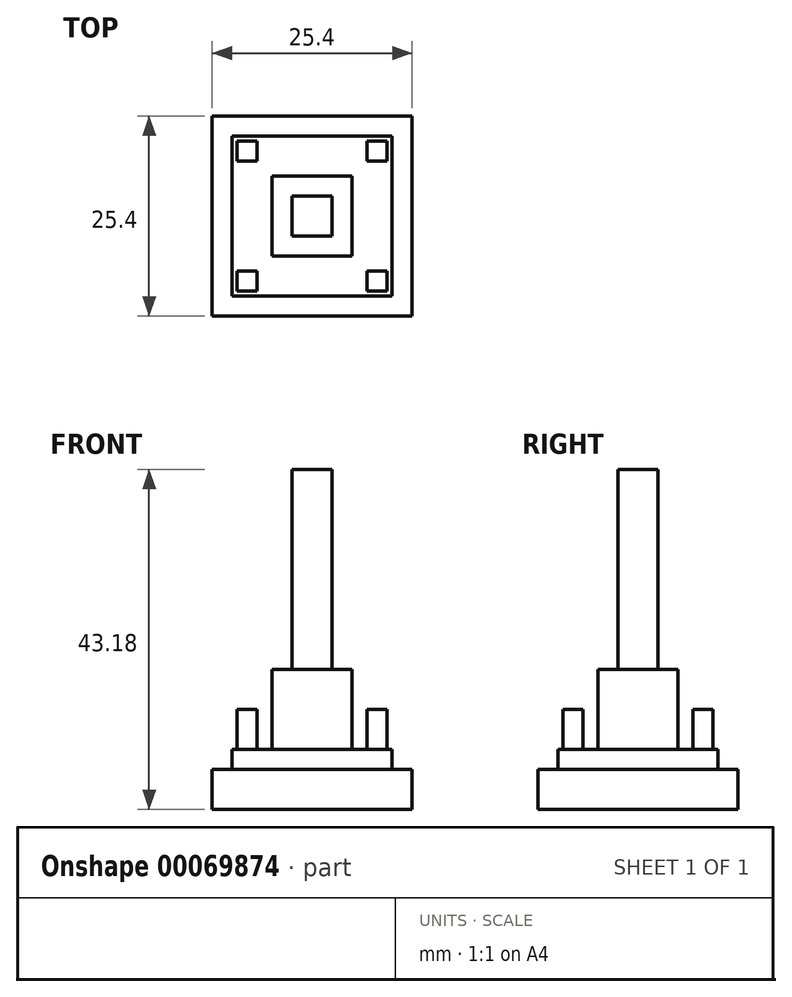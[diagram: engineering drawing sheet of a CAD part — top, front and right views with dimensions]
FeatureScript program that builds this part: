
annotation { "Feature Type Name" : "Feature", "Feature Type Description" : "" }
export const myFeature = defineFeature(function(context is Context, id is Id, definition is map)
    precondition{}
    {
        {
            var Q0;
            Q0=qCreatedBy(makeId("Top.planeOp"),FACE);
            var sketch = newSketch(context, id + "F0", { "sketchPlane" : qUnion([Q0])});
            skLineSegment(sketch, "E0.bottom", {"start": v(0, 0) * mm, "end": v(25.4, 0) * mm});
            skLineSegment(sketch, "E0.top", {"start": v(0, -25.4) * mm, "end": v(25.4, -25.4) * mm});
            skLineSegment(sketch, "E0.left", {"start": v(0, 0) * mm, "end": v(0, -25.4) * mm});
            skLineSegment(sketch, "E0.right", {"start": v(25.4, 0) * mm, "end": v(25.4, -25.4) * mm});
            skSolve(sketch);
        }
        {
            var Q0;
            Q0 = qSketchRegion(id + "F0", true);
            extrude(context, id + "F1", {"entities" : qUnion([Q0]), "depth" : 5.08 * mm});
        }
        {
            var Q0;
            Q0=makeQuery(id+"F1.opExtrude","CAP_FACE",FACE,{"disambiguationData":[OSD([sQuery(id+"F0.wireOp",EDGE,"E0.bottom"),sQuery(id+"F0.wireOp",EDGE,"E0.top"),sQuery(id+"F0.wireOp",EDGE,"E0.left"),sQuery(id+"F0.wireOp",EDGE,"E0.right")])],"isStart":false});
            var sketch = newSketch(context, id + "F2", { "sketchPlane" : qUnion([Q0])});
            skLineSegment(sketch, "E1.bottom", {"start": v(2.54, -2.54) * mm, "end": v(22.86, -2.54) * mm});
            skLineSegment(sketch, "E1.top", {"start": v(2.54, -22.86) * mm, "end": v(22.86, -22.86) * mm});
            skLineSegment(sketch, "E1.left", {"start": v(2.54, -2.54) * mm, "end": v(2.54, -22.86) * mm});
            skLineSegment(sketch, "E1.right", {"start": v(22.86, -2.54) * mm, "end": v(22.86, -22.86) * mm});
            skSolve(sketch);
        }
        {
            var Q0;
            Q0 = qSketchRegion(id + "F2", true);
            extrude(context, id + "F3", {"entities" : qUnion([Q0]), "operationType" : NewBodyOperationType.ADD, "depth" : 2.54 * mm});
        }
        {
            var Q0;
            Q0=makeQuery(id+"F3.opExtrude","CAP_FACE",FACE,{"disambiguationData":[OSD([sQuery(id+"F2.wireOp",EDGE,"E1.bottom"),sQuery(id+"F2.wireOp",EDGE,"E1.top"),sQuery(id+"F2.wireOp",EDGE,"E1.left"),sQuery(id+"F2.wireOp",EDGE,"E1.right")])],"isStart":false});
            var sketch = newSketch(context, id + "F4", { "sketchPlane" : qUnion([Q0])});
            skLineSegment(sketch, "E2.bottom", {"start": v(7.62, -17.78) * mm, "end": v(17.78, -17.78) * mm});
            skLineSegment(sketch, "E2.top", {"start": v(7.62, -7.62) * mm, "end": v(17.78, -7.62) * mm});
            skLineSegment(sketch, "E2.left", {"start": v(7.62, -17.78) * mm, "end": v(7.62, -7.62) * mm});
            skLineSegment(sketch, "E2.right", {"start": v(17.78, -17.78) * mm, "end": v(17.78, -7.62) * mm});
            skSolve(sketch);
        }
        {
            var Q0;
            Q0 = qSketchRegion(id + "F4", true);
            extrude(context, id + "F5", {"entities" : qUnion([Q0]), "operationType" : NewBodyOperationType.ADD, "depth" : 10.16 * mm});
        }
        {
            var Q0;
            Q0=makeQuery(id+"F5.opExtrude","CAP_FACE",FACE,{"disambiguationData":[OSD([sQuery(id+"F4.wireOp",EDGE,"E2.bottom"),sQuery(id+"F4.wireOp",EDGE,"E2.top"),sQuery(id+"F4.wireOp",EDGE,"E2.left"),sQuery(id+"F4.wireOp",EDGE,"E2.right")])],"isStart":false});
            var sketch = newSketch(context, id + "F6", { "sketchPlane" : qUnion([Q0])});
            skLineSegment(sketch, "E3.bottom", {"start": v(10.16, -15.24) * mm, "end": v(15.24, -15.24) * mm});
            skLineSegment(sketch, "E3.top", {"start": v(10.16, -10.16) * mm, "end": v(15.24, -10.16) * mm});
            skLineSegment(sketch, "E3.left", {"start": v(10.16, -15.24) * mm, "end": v(10.16, -10.16) * mm});
            skLineSegment(sketch, "E3.right", {"start": v(15.24, -15.24) * mm, "end": v(15.24, -10.16) * mm});
            skSolve(sketch);
        }
        {
            var Q0;
            Q0 = qSketchRegion(id + "F6", true);
            extrude(context, id + "F7", {"entities" : qUnion([Q0]), "operationType" : NewBodyOperationType.ADD, "depth" : 25.4 * mm});
        }
        {
            var Q0;
            Q0=makeQuery(id+"F3.opExtrude","CAP_FACE",FACE,{"disambiguationData":[OSD([sQuery(id+"F2.wireOp",EDGE,"E1.bottom"),sQuery(id+"F2.wireOp",EDGE,"E1.top"),sQuery(id+"F2.wireOp",EDGE,"E1.left"),sQuery(id+"F2.wireOp",EDGE,"E1.right")])],"isStart":false});
            var sketch = newSketch(context, id + "F8", { "sketchPlane" : qUnion([Q0])});
            skLineSegment(sketch, "E4.bottom", {"start": v(3.17, -3.18) * mm, "end": v(5.71, -3.18) * mm});
            skLineSegment(sketch, "E4.top", {"start": v(3.17, -5.72) * mm, "end": v(5.71, -5.72) * mm});
            skLineSegment(sketch, "E4.left", {"start": v(3.17, -3.18) * mm, "end": v(3.17, -5.72) * mm});
            skLineSegment(sketch, "E4.right", {"start": v(5.71, -3.18) * mm, "end": v(5.71, -5.72) * mm});
            skLineSegment(sketch, "E5.bottom", {"start": v(22.22, -3.18) * mm, "end": v(19.68, -3.18) * mm});
            skLineSegment(sketch, "E5.top", {"start": v(22.22, -5.72) * mm, "end": v(19.68, -5.72) * mm});
            skLineSegment(sketch, "E5.left", {"start": v(22.22, -3.18) * mm, "end": v(22.22, -5.72) * mm});
            skLineSegment(sketch, "E5.right", {"start": v(19.68, -3.18) * mm, "end": v(19.68, -5.72) * mm});
            skLineSegment(sketch, "E6.bottom", {"start": v(22.22, -22.23) * mm, "end": v(19.68, -22.23) * mm});
            skLineSegment(sketch, "E6.top", {"start": v(22.22, -19.69) * mm, "end": v(19.68, -19.69) * mm});
            skLineSegment(sketch, "E6.left", {"start": v(22.22, -22.23) * mm, "end": v(22.22, -19.69) * mm});
            skLineSegment(sketch, "E6.right", {"start": v(19.68, -22.23) * mm, "end": v(19.68, -19.69) * mm});
            skLineSegment(sketch, "E7.bottom", {"start": v(3.17, -22.23) * mm, "end": v(5.71, -22.23) * mm});
            skLineSegment(sketch, "E7.top", {"start": v(3.17, -19.69) * mm, "end": v(5.71, -19.69) * mm});
            skLineSegment(sketch, "E7.left", {"start": v(3.17, -22.23) * mm, "end": v(3.17, -19.69) * mm});
            skLineSegment(sketch, "E7.right", {"start": v(5.71, -22.23) * mm, "end": v(5.71, -19.69) * mm});
            skSolve(sketch);
        }
        {
            var Q0;
            Q0 = qSketchRegion(id + "F8", true);
            extrude(context, id + "F9", {"entities" : qUnion([Q0]), "operationType" : NewBodyOperationType.ADD, "depth" : 5.08 * mm});
        }
        {
            var Q0;
            Q0=makeQuery(id+"F9.opExtrude","SWEPT_FACE",FACE,{"disambiguationData":[OSD([sQuery(id+"F8.wireOp",EDGE,"E7.bottom")])]});
            var sketch = newSketch(context, id + "F10", { "sketchPlane" : qUnion([Q0])});
            skCircle(sketch, "E8", {"center": v(4.44, 11.43) * mm, "radius": 0.64 * mm});
            skSolve(sketch);
        }
        {
            var Q0;
            Q0 = qSketchRegion(id + "F10", true);
            extrude(context, id + "F11", {"entities" : qUnion([Q0]), "operationType" : NewBodyOperationType.ADD, "depth" : 0.25 * mm});
        }
        {
            var Q0;
            Q0=makeQuery(id+"F11.opExtrude","CAP_EDGE",EDGE,{"disambiguationData":[OSD([sQuery(id+"F10.wireOp",EDGE,"E8")])],"isStart":false});
            fillet(context, id + "F12", {"entities" : qUnion([Q0]), "radius" : 0.86 * mm, "tangentPropagation" : true, "allowEdgeOverflow" : false});
        }
        {
            var Q0;
            Q0=makeQuery(id+"F9.opExtrude","SWEPT_FACE",FACE,{"disambiguationData":[OSD([sQuery(id+"F8.wireOp",EDGE,"E7.bottom")])]});
            var sketch = newSketch(context, id + "F13", { "sketchPlane" : qUnion([Q0])});
            skCircle(sketch, "E9", {"center": v(4.44, 11.43) * mm, "radius": 2.2 * mm});
            skSolve(sketch);
        }
        {
            var Q0;
            Q0 = qSketchRegion(id + "F13", true);
            extrude(context, id + "F14", {"entities" : qUnion([Q0]), "operationType" : NewBodyOperationType.REMOVE, "depth" : 25.4 * mm});
        }
    });
